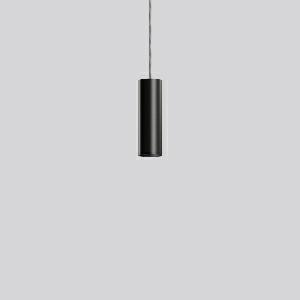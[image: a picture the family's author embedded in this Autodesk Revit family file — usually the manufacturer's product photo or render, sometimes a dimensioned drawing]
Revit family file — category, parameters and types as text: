
# Revit family: deecos_p_micro_911490_003_1_5fbb
name_source: partatom
category: Lighting Fixtures
units: mm (PartAtom-declared; Revit-internal decimal feet)

## family parameters
Cut with Voids When Loaded = No
Host = Face
Light Source = No
Part Type = Normal
Room Calculation Point = No
Round Connector Dimension = Use Diameter
Shared = No

## types (1)
- DEECOS P micro (1 x LED Modul 930, 1250 lm, 3000)
    Apparent Load = 16 VA
    CIE Flux Codes = 92 99 100 100 100
    Color Rendering = 90
    Color Temperature = 3000
    Default Elevation = 1800 mm
    Description = Series: DEECOS P micro
Cylindrical pendant luminaire. Housing: die-cast aluminium, powder-coated. Canopy made of powder-coated sheet steel with magnetic attachment. Optical assembly with lens made of plastic (polycarbonate) for the best homogeneous light distribution - can be changed without tools. Black plastic ring and recessed LED to prevent glare from the side. Best colour rendering index Ra>90. Transparent suspension cable 3 m, can be shortened. High quality converter without flickering and stroboscopic effect. 
Colour: deep black, matt (RAL 9005)
Diameter: 60 mm
Height: 190 mm
Suspension length: 3000 mm
Lamp: LED
Socket: without socket
Colour temperature: 3000K
Colour rendering index (CRI): 92
System power: 16 W
Rated luminous flux: 1250 lm
Luminous efficiency: 78 lm/W
Control gear: Regulated power supply
Protection class: I
Type of protection: IP 20
    Height = 190 mm  [stored 0.62336 ft]
    Lamp = 1 x LED Modul 930
    Lamp Light Flux = 1250 lm
    Lamp count = 1
    Length = 60 mm  [stored 0.19685 ft]
    Lifetime = 50000 h
    Luminous efficacy = 78 lm/W
    Manufacturer = RZB
    ModVariant = No
    Model = 911490.003.1
    Mounting Place = Ceiling
    Mounting Type = Pendant
    Number of Poles = 1
    OnlyDefault = Yes
    Power Factor = 1
    Product Name = DEECOS P micro
    Product group = Pendant luminaires
    ProductGroupID = 902
    Protection Class = Protection class I
    Protection Degree = Degree of protection
    RLX_Detail_Level = 1
    RLX_Emergency_Light_Flux = 0 lm
    RLX_Emergency_Type = 0
    RLX_Emergency_Type_DB = No
    RlxData = <blob elided: 31749 chars, md5=e5c62ce3>
    Socket = socket
    Standby Power = 0 W
    System Light Flux = 1250 lm
    System Power = 16 W
    Type Comments = Product without accessories
    Type Image = 911489.003.jpg
    URL = http://relux.com
    VarID = ---
    Voltage = 0 V
    Weight = 0.00 kg
    Width = 0 mm  [stored 0 ft]

note: [stored X ft] marks values corroborated as IEEE doubles in the binary element streams (Revit-internal decimal feet)

## geometry (parser evidence)
native form markers: Blend x4, Sweep x10
no freeform markers — native parametric forms only
